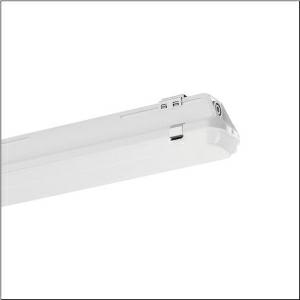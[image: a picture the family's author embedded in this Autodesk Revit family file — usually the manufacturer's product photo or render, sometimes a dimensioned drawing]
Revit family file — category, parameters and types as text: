
# Revit family: monsun_11_51fp10dp460l007
name_source: partatom
category: Lighting Fixtures
units: mm (PartAtom-declared; Revit-internal decimal feet)

## family parameters
Cut with Voids When Loaded = No
Host = Face
Light Source = No
Part Type = Normal
Room Calculation Point = No
Round Connector Dimension = Use Diameter
Shared = No

## types (1)
- --- (1 x LED, 6050 lm, 31.5 W, 4000K)
    Apparent Load = 32 VA
    CIE Flux Codes = 47 77 93 94 100
    Color Rendering = 80
    Color Temperature = 4000K
    Default Elevation = 1800 mm
    Description = Monsun 11, damp-proof luminaire, chain hanger, primary optical cover: enclosure, of PMMA, light emission: direct distribution, primary light characteristic: symmetric, installation type: suspended mounting, surface-mounted, horizontal mounting, vertical mounting, LED, rated luminous flux: 6.050lm, luminous efficacy: 192lm/W, light colour: 840, colour temperature: 4000K, control gear: DALI 2, with terminal, 5-pole, max. 2.5mm², through-wiring: 7x 2.5mm², mains connection: 220..240V, AC, 50/60Hz, rated input power: 32W, housing, of glass-fibre reinforced polyester, uncoated, bright grey, incl. chain hanger, length: 1.590mm, width: 90mm, height: 88mm, clip for enclosure, of stainless steel (V2A), ceiling mounting element, of stainless steel (V2A), chain hanger, of stainless steel (V2A), protection rating (complete): IP66, insulation class (complete): insulation class I (protective earthing), certification: CE, ENEC, VDE, UKCA, protection symbol: D, impact resistance: IK04, permissible operating ambient temperature: -25..+30°C, standard: EN 50419, EN 60598-2-1, corresponds to IFS (International Featured Standards) requirements for safety and quality in the food industry, for indoor or canopied outdoor use, no direct snow, no direct sun, no direct rain, LABS conformity tested according to VDMA 24364:2018-05, contact your sales advisor before using the luminaires in applications with unclear chemical exposure, large temperature fluctuations or condensation-forming humidity, packaging unit: 1 piece
    Height = 89 mm
    Lamp = 1 x LED
    Lamp Light Flux = 6050 lm
    Lamp Power = 31.5 W
    Lamp count = 1
    Length = 1590 mm
    Luminous efficacy = 192 lm/W
    Manufacturer = Siteco
    ModVariant = No
    Model = 51FP10DP460L007
    Mounting Place = Ceiling
    Mounting Type = Surface mounted
    Number of Poles = 1
    OnlyDefault = Yes
    Power Factor = 1
    Product Name = Monsun 11
    Product group = damp-proof luminaire
    ProductGroupID = 300
    Protection Class = Protection class I
    Protection Degree = IP 66
    RLX_Detail_Level = 1
    RLX_Emergency_Light_Flux = 0 lm
    RLX_Emergency_Type = 0
    RLX_Emergency_Type_DB = No
    RlxData = <blob elided: 92341 chars, md5=2ea84fe6>
    Socket = socket
    Standby Power = 0 W
    System Light Flux = 6050 lm
    System Power = 32 W
    Type Comments = factory setting: luminous flux: 100 % | dim-lin: 254 | 219 mA
    Type Image = l_1349237.jpg
    URL = http://relux.com
    VarID = @adj_033983
    Voltage = 0 V
    Weight = 0.00 kg
    Width = 90 mm

## geometry (parser evidence)
native form markers: Blend x4, Sweep x12
no freeform markers — native parametric forms only
